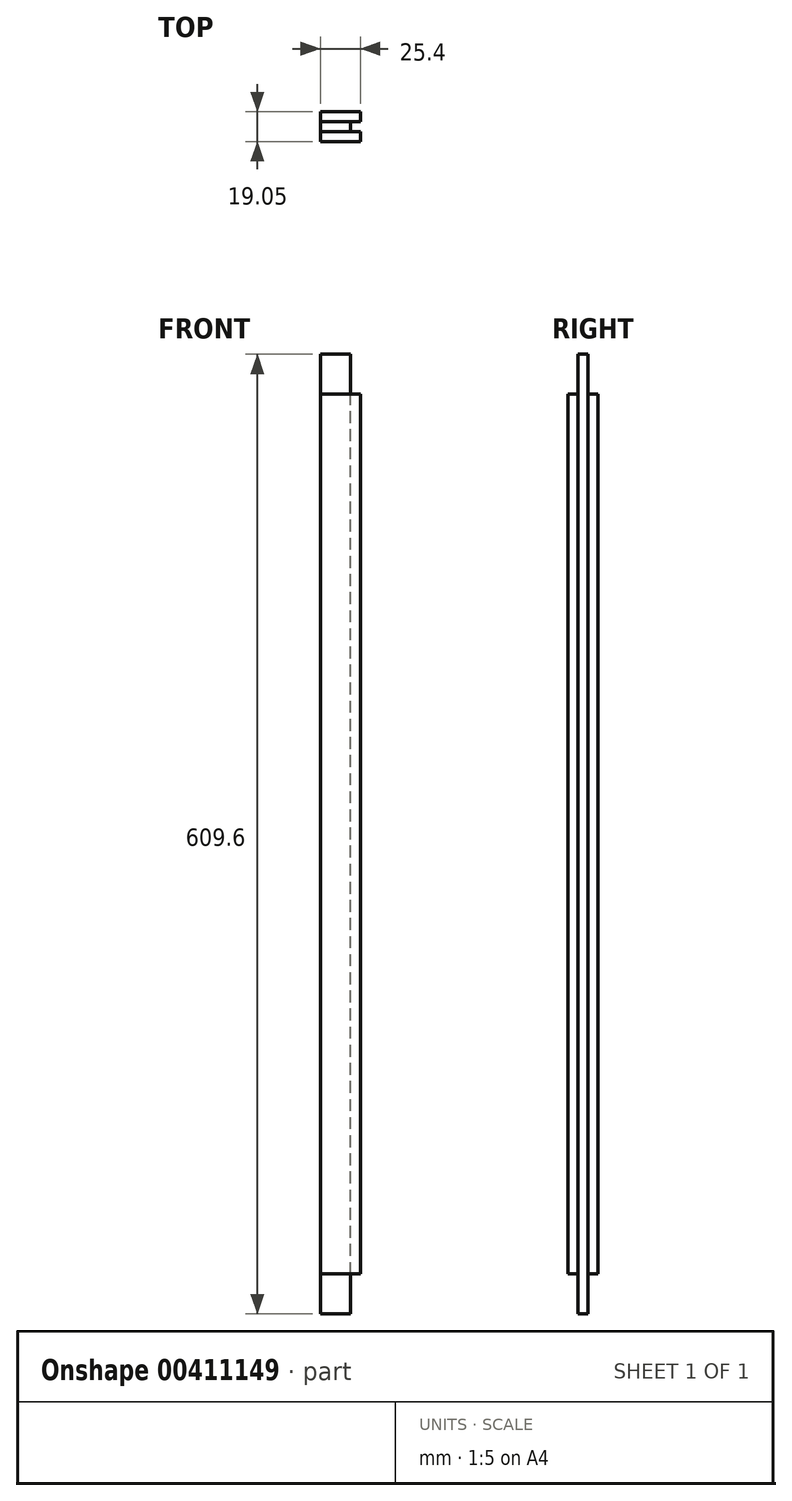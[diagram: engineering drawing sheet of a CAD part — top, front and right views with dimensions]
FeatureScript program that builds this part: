
annotation { "Feature Type Name" : "Feature", "Feature Type Description" : "" }
export const myFeature = defineFeature(function(context is Context, id is Id, definition is map)
    precondition{}
    {
        {
            var Q0;
            Q0=qCreatedBy(makeId("Right.planeOp"),FACE);
            var sketch = newSketch(context, id + "F0", { "sketchPlane" : qUnion([Q0])});
            skLineSegment(sketch, "E0.bottom", {"start": v(0, 0) * mm, "end": v(19.05, 0) * mm});
            skLineSegment(sketch, "E0.top", {"start": v(0, -558.8) * mm, "end": v(19.05, -558.8) * mm});
            skLineSegment(sketch, "E0.left", {"start": v(0, 0) * mm, "end": v(0, -558.8) * mm});
            skLineSegment(sketch, "E0.right", {"start": v(19.05, 0) * mm, "end": v(19.05, -558.8) * mm});
            skLineSegment(sketch, "E1.bottom", {"start": v(6.35, 25.4) * mm, "end": v(12.7, 25.4) * mm});
            skLineSegment(sketch, "E1.top", {"start": v(6.35, -584.2) * mm, "end": v(12.7, -584.2) * mm});
            skLineSegment(sketch, "E1.left", {"start": v(6.35, 25.4) * mm, "end": v(6.35, -584.2) * mm});
            skLineSegment(sketch, "E1.right", {"start": v(12.7, 25.4) * mm, "end": v(12.7, -584.2) * mm});
            skLineSegment(sketch, "E2", {"start": v(9.53, 63.4) * mm, "end": v(9.53, -185.09) * mm, "construction": true});
            skPoint(sketch, "E2.startSnap0", {"position": v(9.53, 0) * mm});
            skSolve(sketch);
        }
        {
            var Q0;
            Q0 = qSketchRegion(id + "F0", true);
            extrude(context, id + "F1", {"entities" : qUnion([Q0]), "depth" : 25.4 * mm});
        }
        {
            var Q0;
            Q0=makeQuery(id+"F1.opExtrude","SWEPT_FACE",FACE,{"disambiguationData":[OSD([sQuery(id+"F0.wireOp",EDGE,"E1.bottom")])]});
            var sketch = newSketch(context, id + "F2", { "sketchPlane" : qUnion([Q0])});
            skLineSegment(sketch, "E3.bottom", {"start": v(25.4, 12.7) * mm, "end": v(19.05, 12.7) * mm});
            skLineSegment(sketch, "E3.top", {"start": v(25.4, 6.35) * mm, "end": v(19.05, 6.35) * mm});
            skLineSegment(sketch, "E3.left", {"start": v(25.4, 12.7) * mm, "end": v(25.4, 6.35) * mm});
            skLineSegment(sketch, "E3.right", {"start": v(19.05, 12.7) * mm, "end": v(19.05, 6.35) * mm});
            skSolve(sketch);
        }
        {
            var Q0;
            Q0 = qSketchRegion(id + "F2", true);
            extrude(context, id + "F3", {"entities" : qUnion([Q0]), "operationType" : NewBodyOperationType.REMOVE, "endBound" : BoundingType.THROUGH_ALL, "oppositeDirection" : true, "depth" : 25.4 * mm});
        }
    });
